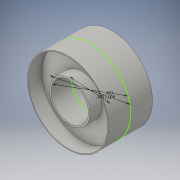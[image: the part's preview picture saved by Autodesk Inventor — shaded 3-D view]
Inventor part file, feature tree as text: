
AUTODESK INVENTOR PART (.ipt)
format: ipt  version: 2016 (Build 200138000, 138)  size: 129,024 bytes
history: native  units: in
note: dims shown in document units (in); Inventor stores cm internally (conversion verified against a paired STEP export)
features: extrude x4, sketch x1, fillet x1
ambient origin geometry x8: Origin, YZ Plane, XZ Plane, XY Plane, X Axis, Y Axis, Z Axis, Center Point
bodies: Solid1 (feature_tree)
feature tree (6):
  sketch  "Sketch1"  dims[d1=1.0in d2=0.98in d3=0.5in d4=0.24in d5=0.24in d6=0.0in d7=0.0in d8=0.27in d9=0.27in d10=0.0in d11=0.0in d12=0.1in d13=0.1in d14=0.0in d15=0.0in d16=0.25in d17=0.25in d18=0.0in d19=0.0in d20=0.001in]
  extrude  "Extrusion1"  Depth=0.25in
  extrude  "Extrusion2"  Depth=0.5in
  extrude  "Extrusion3"  Depth=0.25in TaperAngle=0.0deg
  extrude  "Extrusion4"  Depth=0.27in TaperAngle=0.0deg
  fillet  "Fillet1"  Radius=0.1in
